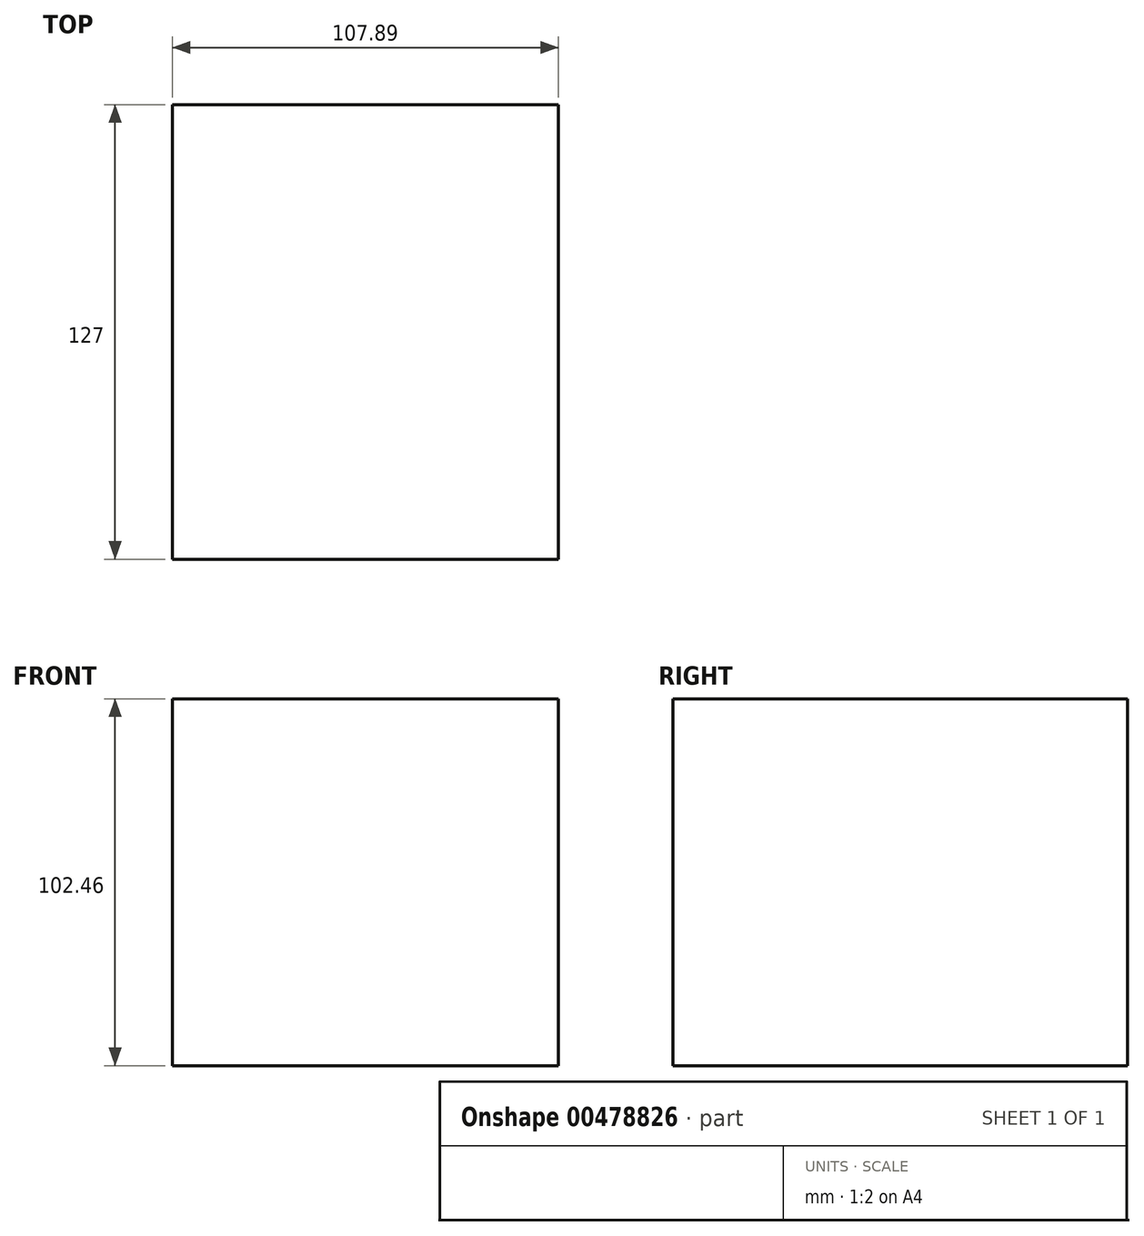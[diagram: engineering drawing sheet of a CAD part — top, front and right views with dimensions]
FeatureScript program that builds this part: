
annotation { "Feature Type Name" : "Feature", "Feature Type Description" : "" }
export const myFeature = defineFeature(function(context is Context, id is Id, definition is map)
    precondition{}
    {
        {
            var Q0;
            Q0=qCreatedBy(makeId("Front.planeOp"),FACE);
            var sketch = newSketch(context, id + "F0", { "sketchPlane" : qUnion([Q0])});
            skLineSegment(sketch, "E0.bottom", {"start": v(-53.17, 48.78) * mm, "end": v(54.72, 48.78) * mm});
            skLineSegment(sketch, "E0.top", {"start": v(-53.17, -53.68) * mm, "end": v(54.72, -53.68) * mm});
            skLineSegment(sketch, "E0.left", {"start": v(-53.17, 48.78) * mm, "end": v(-53.17, -53.68) * mm});
            skLineSegment(sketch, "E0.right", {"start": v(54.72, 48.78) * mm, "end": v(54.72, -53.68) * mm});
            skSolve(sketch);
        }
        {
            var Q0;
            Q0=makeQuery(id+"F0.imprint","IMPRINT",FACE,{"disambiguationData":[TD([[makeQuery(id+"F0.imprint","IMPRINT",EDGE,{"derivedFrom":sQuery(id+"F0.wireOp",EDGE,"E0.bottom")}),-1.0]])]});
            extrude(context, id + "F1", {"entities" : qUnion([Q0]), "depth" : 127 * mm});
        }
    });
